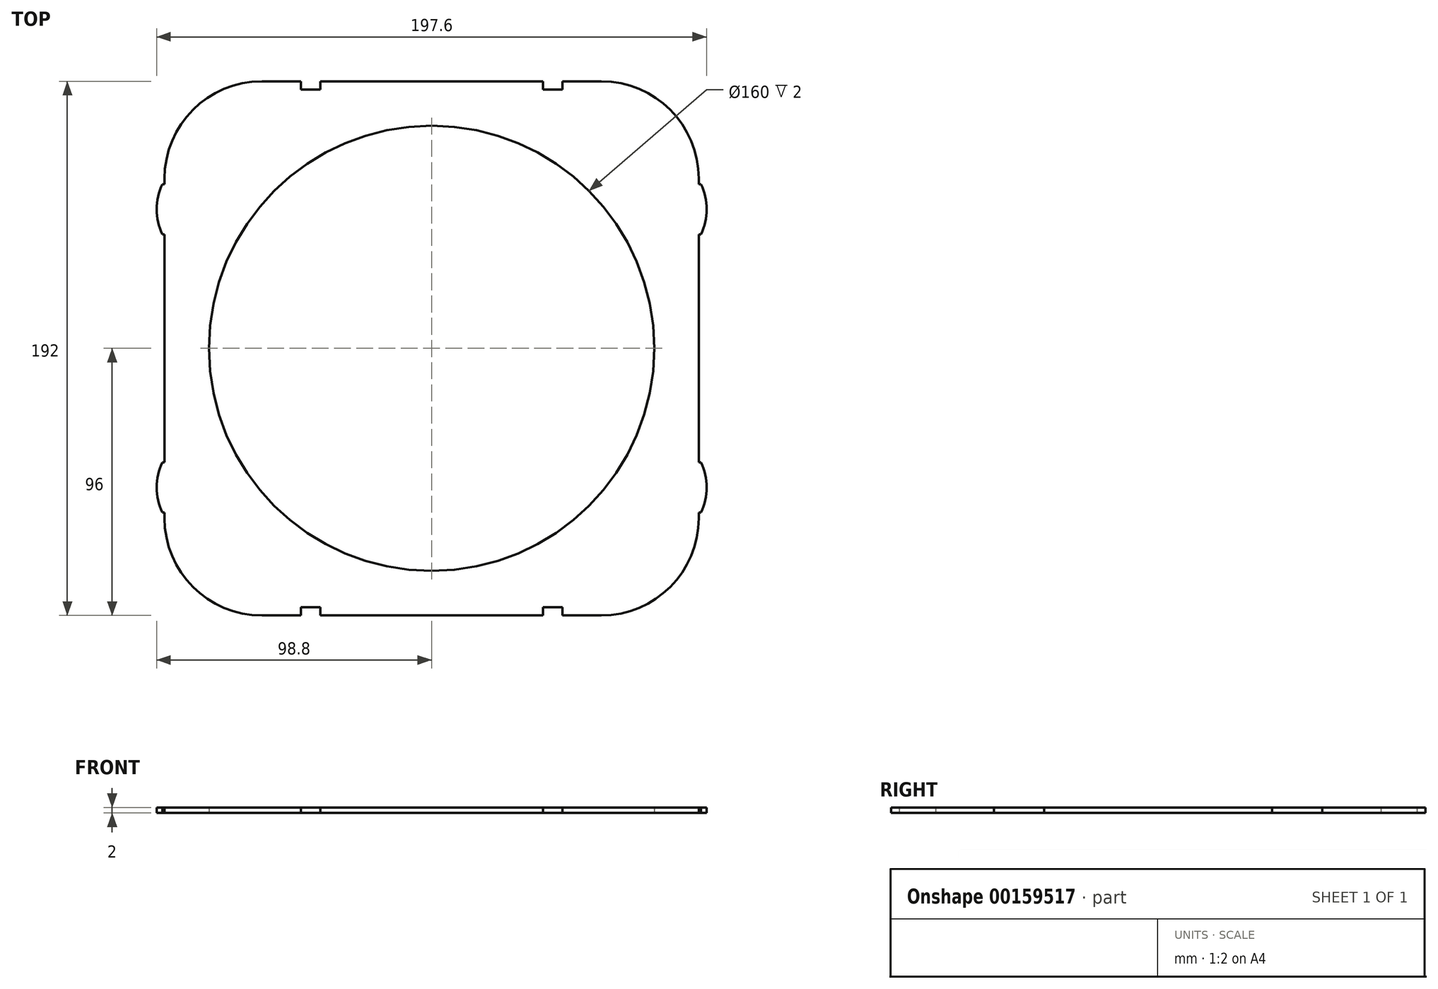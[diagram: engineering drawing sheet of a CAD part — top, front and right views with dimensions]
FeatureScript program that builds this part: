
annotation { "Feature Type Name" : "Feature", "Feature Type Description" : "" }
export const myFeature = defineFeature(function(context is Context, id is Id, definition is map)
    precondition{}
    {
        {
            var Q0;
            Q0=qCreatedBy(makeId("Top.planeOp"),FACE);
            var sketch = newSketch(context, id + "F0", { "sketchPlane" : qUnion([Q0])});
            skLineSegment(sketch, "E0.bottom", {"start": v(61, 96) * mm, "end": v(47, 96) * mm});
            skLineSegment(sketch, "E0.top", {"start": v(61, -96) * mm, "end": v(47, -96) * mm});
            skLineSegment(sketch, "E0.left", {"start": v(96, 61) * mm, "end": v(96, 41) * mm});
            skLineSegment(sketch, "E0.right", {"start": v(-96, 61) * mm, "end": v(-96, 41) * mm});
            skPoint(sketch, "E0.middle", {"position": v(0, 0) * mm});
            skCircle(sketch, "E1", {"center": v(0, 0) * mm, "radius": 80 * mm});
            skPoint(sketch, "E2.middle", {"position": v(-96, 0) * mm});
            skLineSegment(sketch, "E3.trimOffspring", {"start": v(-96, -41) * mm, "end": v(-96, -61) * mm});
            skLineSegment(sketch, "E4.trimOffspring", {"start": v(96, -41) * mm, "end": v(96, -61) * mm});
            skLineSegment(sketch, "E5.bottom", {"start": v(-96, 59) * mm, "end": v(-96.8, 59) * mm});
            skLineSegment(sketch, "E5.top", {"start": v(-96, 41) * mm, "end": v(-96.8, 41) * mm});
            skLineSegment(sketch, "E5.left", {"start": v(-96, 59) * mm, "end": v(-96, 41) * mm});
            skLineSegment(sketch, "E5.right", {"start": v(-96.8, 59) * mm, "end": v(-96.8, 41) * mm});
            skPoint(sketch, "E6", {"position": v(-96.8, 50) * mm});
            skLineSegment(sketch, "E7.MirrorCS", {"start": v(-96, -59) * mm, "end": v(-96.8, -59) * mm});
            skLineSegment(sketch, "E8.MirrorCS", {"start": v(-96.8, -59) * mm, "end": v(-96.8, -41) * mm});
            skLineSegment(sketch, "E9.MirrorCS", {"start": v(-96, -41) * mm, "end": v(-96.8, -41) * mm});
            skPoint(sketch, "E10", {"position": v(-96.8, -50) * mm});
            skPoint(sketch, "E11", {"position": v(-98.8, 50) * mm});
            skArc(sketch, "E12", {"start": v(-96.8, 59) * mm, "mid": v(-98.8, 50) * mm, "end": v(-96.8, 41) * mm});
            skArc(sketch, "E13.MirrorCS", {"start": v(-96.8, -59) * mm, "mid": v(-98.8, -50) * mm, "end": v(-96.8, -41) * mm});
            skLineSegment(sketch, "E14.MirrorCS", {"start": v(96, 59) * mm, "end": v(96.8, 59) * mm});
            skArc(sketch, "E15.MirrorCS", {"start": v(96.8, 59) * mm, "mid": v(98.8, 50) * mm, "end": v(96.8, 41) * mm});
            skLineSegment(sketch, "E16.MirrorCS", {"start": v(96, 41) * mm, "end": v(96.8, 41) * mm});
            skLineSegment(sketch, "E17.MirrorCS", {"start": v(96, -41) * mm, "end": v(96.8, -41) * mm});
            skArc(sketch, "E18.MirrorCS", {"start": v(96.8, -59) * mm, "mid": v(98.8, -50) * mm, "end": v(96.8, -41) * mm});
            skLineSegment(sketch, "E19.MirrorCS", {"start": v(96, -59) * mm, "end": v(96.8, -59) * mm});
            skLineSegment(sketch, "E20", {"start": v(-96, 41) * mm, "end": v(-96, -41) * mm});
            skLineSegment(sketch, "E21", {"start": v(96, 41) * mm, "end": v(96, -41) * mm});
            skLineSegment(sketch, "E22.top", {"start": v(-47, 93) * mm, "end": v(-40, 93) * mm});
            skLineSegment(sketch, "E22.left", {"start": v(-47, 96) * mm, "end": v(-47, 93) * mm});
            skLineSegment(sketch, "E22.right", {"start": v(-40, 96) * mm, "end": v(-40, 93) * mm});
            skLineSegment(sketch, "E23.trimOffspring", {"start": v(-47, 96) * mm, "end": v(-61, 96) * mm});
            skLineSegment(sketch, "E24.MirrorCS", {"start": v(47, 96) * mm, "end": v(47, 93) * mm});
            skLineSegment(sketch, "E25.MirrorCS", {"start": v(47, 93) * mm, "end": v(40, 93) * mm});
            skLineSegment(sketch, "E26.MirrorCS", {"start": v(40, 96) * mm, "end": v(40, 93) * mm});
            skLineSegment(sketch, "E27.MirrorCS", {"start": v(-47, -96) * mm, "end": v(-47, -93) * mm});
            skLineSegment(sketch, "E28.MirrorCS", {"start": v(-47, -93) * mm, "end": v(-40, -93) * mm});
            skLineSegment(sketch, "E29.MirrorCS", {"start": v(-40, -96) * mm, "end": v(-40, -93) * mm});
            skLineSegment(sketch, "E30.MirrorCS", {"start": v(40, -96) * mm, "end": v(40, -93) * mm});
            skLineSegment(sketch, "E31.MirrorCS", {"start": v(47, -93) * mm, "end": v(40, -93) * mm});
            skLineSegment(sketch, "E32.MirrorCS", {"start": v(47, -96) * mm, "end": v(47, -93) * mm});
            skLineSegment(sketch, "E33.trimOffspring", {"start": v(40, 96) * mm, "end": v(-40, 96) * mm});
            skLineSegment(sketch, "E34.trimOffspring", {"start": v(-47, -96) * mm, "end": v(-61, -96) * mm});
            skLineSegment(sketch, "E35.trimOffspring", {"start": v(40, -96) * mm, "end": v(-40, -96) * mm});
            skPoint(sketch, "E36.visualSharp", {"position": v(-96, -96) * mm});
            skArc(sketch, "E36.filletArc", {"start": v(-96, -61) * mm, "mid": v(-85.75, -85.75) * mm, "end": v(-61, -96) * mm});
            skPoint(sketch, "E37.visualSharp", {"position": v(96, -96) * mm});
            skArc(sketch, "E37.filletArc", {"start": v(61, -96) * mm, "mid": v(85.75, -85.75) * mm, "end": v(96, -61) * mm});
            skPoint(sketch, "E38.visualSharp", {"position": v(96, 96) * mm});
            skArc(sketch, "E38.filletArc", {"start": v(96, 61) * mm, "mid": v(85.75, 85.75) * mm, "end": v(61, 96) * mm});
            skPoint(sketch, "E39.visualSharp", {"position": v(-96, 96) * mm});
            skArc(sketch, "E39.filletArc", {"start": v(-61, 96) * mm, "mid": v(-85.75, 85.75) * mm, "end": v(-96, 61) * mm});
            skSolve(sketch);
        }
        {
            var Q0;
            Q0 = qSketchRegion(id + "F0", true);
            extrude(context, id + "F1", {"entities" : qUnion([Q0]), "depth" : 2 * mm});
        }
    });
